# Revit family: Reece_Vanity_St Michel_Kayla
name_source: partatom
category: Casework
revit_build: Autodesk Revit 2018 (Build: 20190510_1515(x64)
units: mm (PartAtom-declared; Revit-internal decimal feet)

## family parameters
Always vertical = Yes
Cut with Voids When Loaded = Yes
Room Calculation Point = Yes
Shared = Yes
Work Plane-Based = Yes

## types (1)
- Reece_All Types
    Default Elevation = 0 mm  [stored 0 ft]
    Description = -
    Disclaimer = THIS FILE IS THE PROPERTY OF THE REECE GROUP. IT MAY NOT BE REPRODUCED, REVERSE-ENGINEERED OR MODIFIED. ANY REPUBLICATION, TRANSMISSION OR DISTRIBUTION FOR THE PURPOSE OF COMMERCIALLY EXPLOITING THE FILES IS PROHIBITED.
    Finish = Please refer to Colour, Finish and Material Variations Document for more information.
    Keynote = Product #, Reece_Vanity_St Michel_Kayla - Reece_All Types
    Manufacturer = St Michel
    Model = Kayla
    Reece_Basin_1_Attachment_Point = Yes
    Reece_Basin_1_Offset_From Side = 300 mm
    Reece_Basin_2_Attachment_Point = No
    Reece_Basin_2_Offset_From Side = 100 mm  [stored 0.328084 ft]
    Reece_Bench Mounted Basin_1 = Yes
    Reece_Bench Mounted Basin_1_Outlet = 0 mm  [stored 0 ft]
    Reece_Bench Mounted Basin_2 = No
    Reece_Bench Mounted Basin_2_Outlet = 0 mm  [stored 0 ft]
    Reece_Bench Mounted Basin_Width Control = 483 mm
    Reece_Benchtop_Bench Mounted Basin = Yes
    Reece_Benchtop_No Basin_Double Bowl = No
    Reece_Benchtop_No Basin_Single Bowl = Yes
    Reece_Benchtop_Thickness = 20.5 mm  [stored 0.0672572 ft]
    Reece_Cabinet_Depth = 495 mm  [stored 1.62402 ft]
    Reece_Cabinet_Height = 400 mm  [stored 1.31234 ft]
    Reece_Cabinet_Width = 1194 mm
    Reece_Centre_Basin = No
    Reece_Cherry Pie_Benchtop_Double Bowl = No
    Reece_Cherry Pie_Benchtop_Single Bowl = No
    Reece_Cutout Hole_Void_Offset_Bench Mounted Basin_1 = -29 mm  [stored -0.0951444 ft]
    Reece_Cutout Hole_Void_Offset_Bench Mounted Basin_2 = 0 mm  [stored 0 ft]
    Reece_Detail_Disclaimer = THIS FILE IS THE PROPERTY OF THE REECE GROUP. IT MAY NOT BE REPRODUCED, REVERSE-ENGINEERED OR MODIFIED. ANY REPUBLICATION, TRANSMISSION OR DISTRIBUTION FOR THE PURPOSE OF COMMERCIALLY EXPLOITING THE FILES IS PROHIBITED.
    Reece_Detail_Installation = Drawer Only
    Reece_Drawer_1_No_Cutout = No
    Reece_Drawer_1_Width = 1158 mm
    Reece_Drawer_1_With_Cutout = Yes
    Reece_Drawer_2 = No
    Reece_Drawer_2_No_Cutout = Yes
    Reece_Drawer_2_Width = 1158 mm
    Reece_Drawer_2_With_Cutout = No
    Reece_Drawer_Right Panel_Offset = 13 mm  [stored 0.0426509 ft]
    Reece_Drawers_Count = 1
    Reece_Integrated Basin Benchtop_Single Bowl = No
    Reece_Integrated Basin_1 = No
    Reece_Integrated Basin_1_Outlet = 0 mm  [stored 0 ft]
    Reece_Integrated Basin_2 = No
    Reece_Integrated Basin_2_Outlet = 0 mm  [stored 0 ft]
    Reece_Integrated Basin_Benchtop_Double Bowl = No
    Reece_Material_Base = Reece_Polyurethane_Matte White
    Reece_Material_Cabinet = Reece_Oak_French
    Reece_Material_Colour = Reece_Brass_Chrome
    Reece_Material_Main = Reece_Cherry Pie_Solid_Surface_Bright White
    Reece_Material_Secondary = Reece_FINECERAMIC_White
    Reece_Overall_Depth = 500 mm  [stored 1.64042 ft]
    Reece_Overall_Height = 420.5 mm
    Reece_Overall_Width = 1200 mm
    Reece_Product_Brand = St Michel
    Reece_Product_Mount = Wall Mounted
    Reece_Product_Sub Brand = Kayla
    Reece_Product_Type = Vanity
    Reece_Right_Basin = No
    Reece_Round Basin = No
    Reece_Round Basin_1_Switch = No
    Reece_Round Basin_2_Switch = No
    Reece_Soft Round Basin_1_Switch = No
    Reece_Soft Round Basin_2_Switch = No
    Reece_Soft Square Basin = No
    Reece_Square Basin = No
    Reece_Square Basin_1_Swtich = No
    Reece_Square Basin_2_Switch = No
    Reece_Taphole_Offset = 60 mm  [stored 0.19685 ft]
    Type Comments = Vanity
    URL = -

note: [stored X ft] marks values corroborated as IEEE doubles in the binary element streams (Revit-internal decimal feet)

## geometry (parser evidence)
native form markers: Sweep x15
no freeform markers — native parametric forms only
